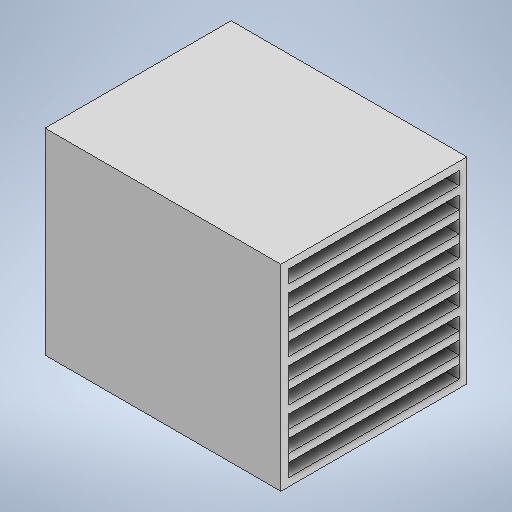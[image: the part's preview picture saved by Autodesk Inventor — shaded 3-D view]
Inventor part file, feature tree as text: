
AUTODESK INVENTOR PART (.ipt)
format: ipt  version: 2025.1 (Build 291241020, 241B)  size: 305,152 bytes
history: native  units: in
note: dims shown in document units (in); Inventor stores cm internally (conversion verified against a paired STEP export)
features: sketch x5, extrude x3
ambient origin geometry x8: Origin, YZ Plane, XZ Plane, XY Plane, X Axis, Y Axis, Z Axis, Center Point
bodies: Solid1 (feature_tree)
feature tree (8):
  extrude  "Extrusion1"  Depth=3.5433in
  sketch  "Sketch2"  dims[d2=0.1181in d3=3.5433in d4=0.1181in d5=3.5433in]
  extrude  "Extrusion2"  Depth=0.1181in
  sketch  "Sketch4"  dims[d10=0.1181in d11=3.5433in]
  extrude  "Extrusion3"  Depth=0.1181in
  sketch  "Sketch1"  dims[d0=0.1181in d1=3.5433in]
  sketch  "Sketch3"  dims[d6=0.1181in d7=3.5433in d8=0.1181in d9=3.5433in]
  sketch  "Sketch5"  dims[d12=0.1181in d13=3.5433in d14=0.1181in d15=3.5433in d16=0.1181in d17=3.5433in d18=0.1181in d19=3.5433in d20=0.1969in d21=0.1969in d22=0.1969in d23=0.1969in d24=0.1969in d25=0.1969in d26=0.1969in d27=0.1969in d28=0.1969in d29=2.5591in d30=0.0in d31=0.1181in d32=0.0in d33=0.1181in d34=0.0in d35=0.7874in d36=3.5433in d37=0.7874in d38=3.5433in]
